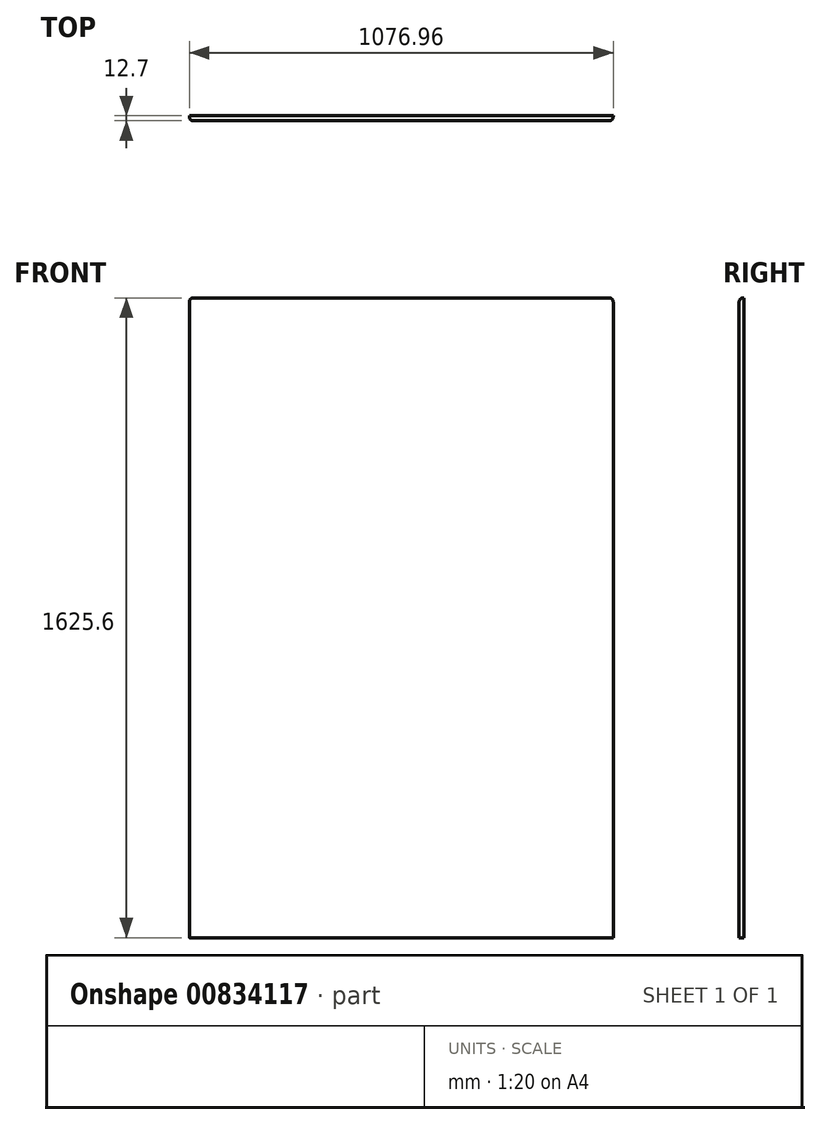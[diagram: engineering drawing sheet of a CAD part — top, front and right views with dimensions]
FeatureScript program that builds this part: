
annotation { "Feature Type Name" : "Feature", "Feature Type Description" : "" }
export const myFeature = defineFeature(function(context is Context, id is Id, definition is map)
    precondition{}
    {
        {
            var Q0;
            Q0=qCreatedBy(makeId("Front.planeOp"),FACE);
            var sketch = newSketch(context, id + "F0", { "sketchPlane" : qUnion([Q0])});
            skLineSegment(sketch, "E0.bottom", {"start": v(538.48, -812.8) * mm, "end": v(-538.48, -812.8) * mm});
            skLineSegment(sketch, "E0.top", {"start": v(538.48, 812.8) * mm, "end": v(-538.48, 812.8) * mm});
            skLineSegment(sketch, "E0.left", {"start": v(538.48, -812.8) * mm, "end": v(538.48, 812.8) * mm});
            skLineSegment(sketch, "E0.right", {"start": v(-538.48, -812.8) * mm, "end": v(-538.48, 812.8) * mm});
            skPoint(sketch, "E0.middle", {"position": v(0, 0) * mm});
            skSolve(sketch);
        }
        {
            var Q0;
            Q0=qSketchRegion(id+"F0",true);
            extrude(context, id + "F1", {"entities" : qUnion([Q0]), "depth" : 12.7 * mm});
        }
        {
            var Q0;
            Q0=makeQuery(id+"F1.opExtrude","CAP_EDGE",EDGE,{"disambiguationData":[OSD([sQuery(id+"F0.wireOp",EDGE,"E0.top")])],"isStart":false});
            fillet(context, id + "F2", {"entities" : qUnion([Q0]), "radius" : 10.16 * mm, "tangentPropagation" : true, "allowEdgeOverflow" : false});
        }
        {
            var Q0;
            Q0=makeQuery(id+"F1.opExtrude","CAP_EDGE",EDGE,{"disambiguationData":[OSD([sQuery(id+"F0.wireOp",EDGE,"E0.left")])],"isStart":false});
            var Q1;
            Q1=makeQuery(id+"F1.opExtrude","CAP_EDGE",EDGE,{"disambiguationData":[OSD([sQuery(id+"F0.wireOp",EDGE,"E0.right")])],"isStart":false});
            fillet(context, id + "F3", {"entities" : qUnion([Q0, Q1]), "radius" : 10.16 * mm, "tangentPropagation" : true, "allowEdgeOverflow" : false});
        }
    });
